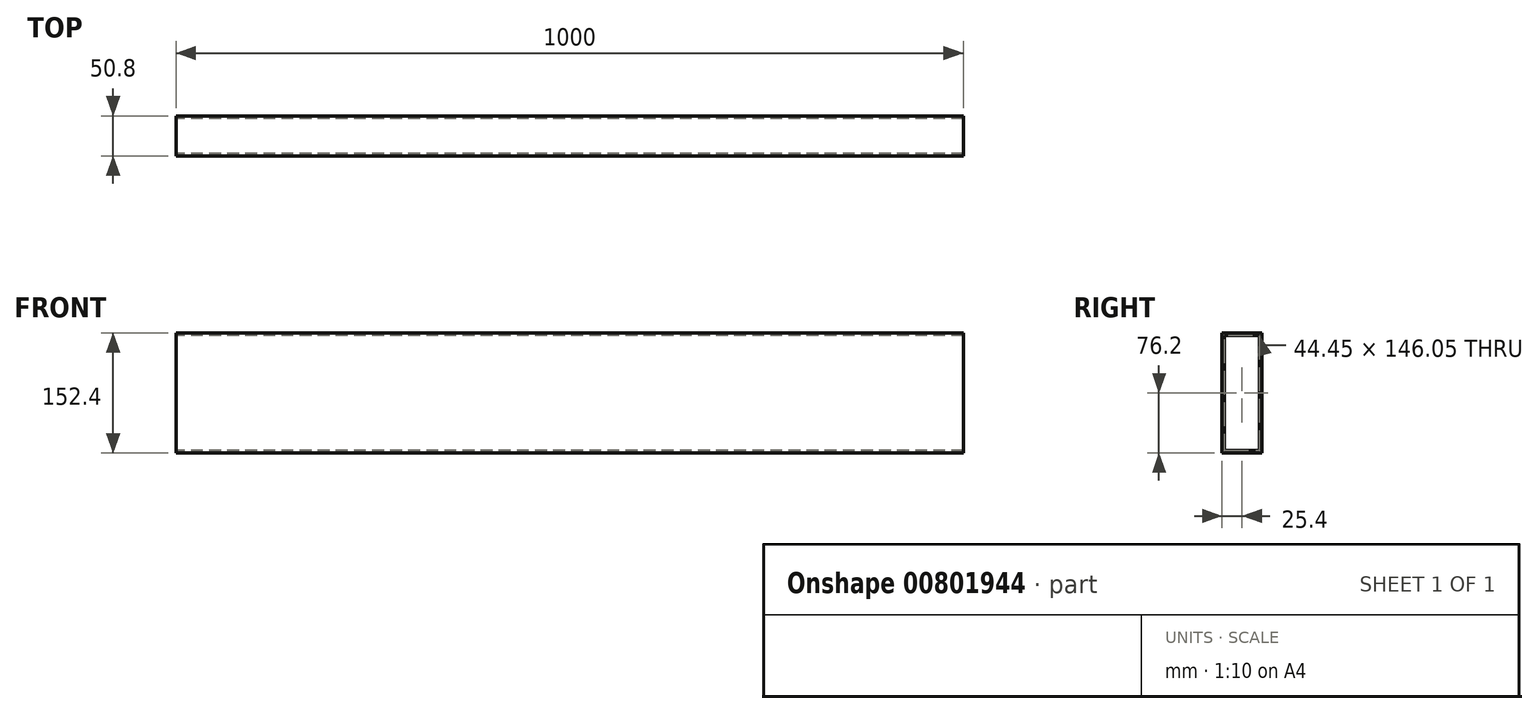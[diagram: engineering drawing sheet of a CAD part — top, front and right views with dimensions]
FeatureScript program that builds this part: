
annotation { "Feature Type Name" : "Feature", "Feature Type Description" : "" }
export const myFeature = defineFeature(function(context is Context, id is Id, definition is map)
    precondition{}
    {
        {
            var Q0;
            Q0=qCreatedBy(makeId("Right.planeOp"),FACE);
            var sketch = newSketch(context, id + "F0", { "sketchPlane" : qUnion([Q0])});
            skLineSegment(sketch, "E0.bottom", {"start": v(25.4, -76.2) * mm, "end": v(-25.4, -76.2) * mm});
            skLineSegment(sketch, "E0.top", {"start": v(25.4, 76.2) * mm, "end": v(-25.4, 76.2) * mm});
            skLineSegment(sketch, "E0.left", {"start": v(25.4, -76.2) * mm, "end": v(25.4, 76.2) * mm});
            skLineSegment(sketch, "E0.right", {"start": v(-25.4, -76.2) * mm, "end": v(-25.4, 76.2) * mm});
            skPoint(sketch, "E0.middle", {"position": v(0, 0) * mm});
            skLineSegment(sketch, "E1.bottom", {"start": v(22.23, -73.03) * mm, "end": v(-22.22, -73.03) * mm});
            skLineSegment(sketch, "E1.top", {"start": v(22.22, 73.02) * mm, "end": v(-22.23, 73.02) * mm});
            skLineSegment(sketch, "E1.left", {"start": v(22.22, -73.02) * mm, "end": v(22.22, 73.02) * mm});
            skLineSegment(sketch, "E1.right", {"start": v(-22.22, -73.02) * mm, "end": v(-22.22, 73.02) * mm});
            skSolve(sketch);
        }
        {
            var Q0;
            Q0 = qSketchRegion(id + "F0", true);
            extrude(context, id + "F1", {"entities" : qUnion([Q0]), "depth" : 1000 * mm, "offsetDistance" : 25 * mm, "symmetric" : true});
        }
    });
